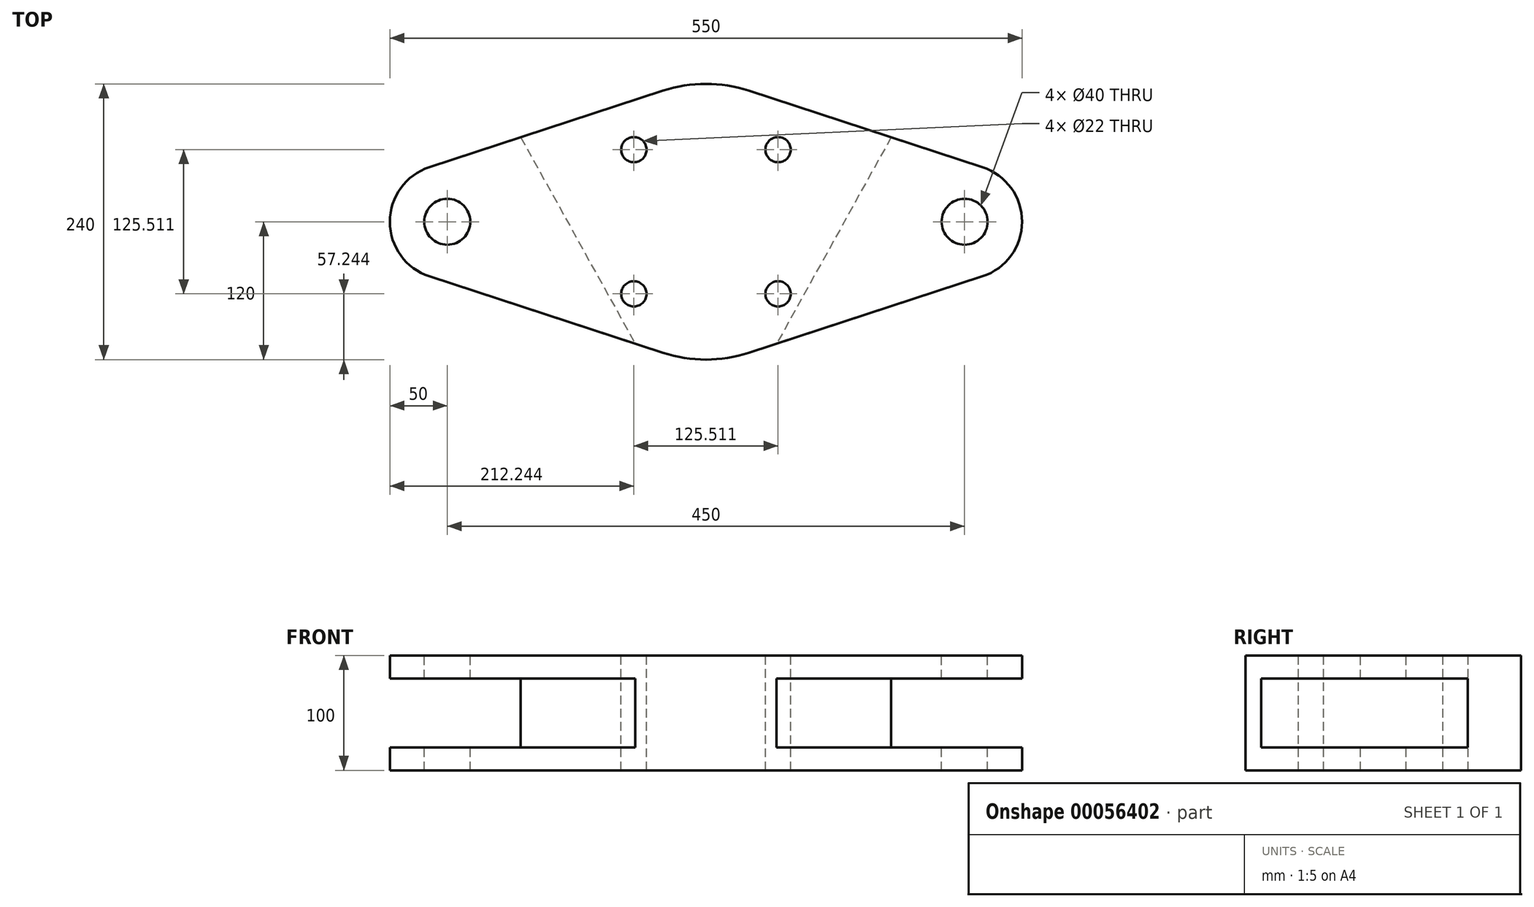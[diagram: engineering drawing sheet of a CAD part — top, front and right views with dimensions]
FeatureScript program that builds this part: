
annotation { "Feature Type Name" : "Feature", "Feature Type Description" : "" }
export const myFeature = defineFeature(function(context is Context, id is Id, definition is map)
    precondition{}
    {
        {
            var Q0;
            Q0=qCreatedBy(makeId("Top.planeOp"),FACE);
            var sketch = newSketch(context, id + "F0", { "sketchPlane" : qUnion([Q0])});
            skArc(sketch, "E0", {"start": v(37.33, 114.04) * mm, "mid": v(0, 120) * mm, "end": v(-37.33, 114.04) * mm});
            skLineSegment(sketch, "E1", {"start": v(0, -118.78) * mm, "end": v(0, 115.8) * mm, "construction": true});
            skArc(sketch, "E2", {"start": v(240.56, -47.52) * mm, "mid": v(275, 0) * mm, "end": v(240.56, 47.52) * mm});
            skLineSegment(sketch, "E3", {"start": v(37.33, 114.04) * mm, "end": v(240.56, 47.52) * mm});
            skLineSegment(sketch, "E4", {"start": v(37.33, -114.04) * mm, "end": v(240.56, -47.52) * mm});
            skLineSegment(sketch, "E5.MirrorCS", {"start": v(-37.33, 114.04) * mm, "end": v(-240.56, 47.52) * mm});
            skArc(sketch, "E6.MirrorCS", {"start": v(-240.56, -47.52) * mm, "mid": v(-275, 0) * mm, "end": v(-240.56, 47.52) * mm});
            skLineSegment(sketch, "E7.MirrorCS", {"start": v(-37.33, -114.04) * mm, "end": v(-240.56, -47.52) * mm});
            skArc(sketch, "E8.trimOffspring", {"start": v(-37.33, -114.04) * mm, "mid": v(0, -120) * mm, "end": v(37.33, -114.04) * mm});
            skLineSegment(sketch, "E9", {"start": v(-225, 0) * mm, "end": v(225, 0) * mm, "construction": true});
            skCircle(sketch, "E10", {"center": v(225, 0) * mm, "radius": 20 * mm});
            skCircle(sketch, "E11", {"center": v(0, 0) * mm, "radius": 88.75 * mm, "construction": true});
            skLineSegment(sketch, "E12", {"start": v(0, 0) * mm, "end": v(79.17, 79.17) * mm, "construction": true});
            skCircle(sketch, "E13", {"center": v(62.76, 62.76) * mm, "radius": 11 * mm});
            skCircle(sketch, "E14.1.0", {"center": v(-62.76, 62.76) * mm, "radius": 11 * mm});
            skCircle(sketch, "E14.2.0", {"center": v(-62.76, -62.76) * mm, "radius": 11 * mm});
            skCircle(sketch, "E14.3.0", {"center": v(62.76, -62.76) * mm, "radius": 11 * mm});
            skPoint(sketch, "E15", {"position": v(61.5, -106.13) * mm});
            skLineSegment(sketch, "E16", {"start": v(61.5, -106.13) * mm, "end": v(170.51, 90.53) * mm, "construction": true});
            skPoint(sketch, "E17.MirrorP", {"position": v(-61.5, -106.13) * mm});
            skLineSegment(sketch, "E18.MirrorCS", {"start": v(-61.5, -106.13) * mm, "end": v(-170.51, 90.53) * mm, "construction": true});
            skCircle(sketch, "E19.MirrorC", {"center": v(-225, 0) * mm, "radius": 20 * mm});
            skSolve(sketch);
        }
        {
            var Q0;
            Q0=makeQuery(id+"F0.imprint","IMPRINT",FACE,{"disambiguationData":[TD([[makeQuery(id+"F0.imprint","IMPRINT",EDGE,{"derivedFrom":sQuery(id+"F0.wireOp",EDGE,"E0")}),1.0]])]});
            extrude(context, id + "F1", {"entities" : qUnion([Q0]), "oppositeDirection" : true, "depth" : 100 * mm});
        }
        {
            var Q0;
            Q0=qCreatedBy(makeId("Right.planeOp"),FACE);
            var Q1;
            Q1=sQuery(id+"F0.wireOp",EDGE,"E16");
            cPlane(context, id + "F2", {"entities" : qUnion([Q0, Q1]), "cplaneType" : CPlaneType.LINE_ANGLE, "offset" : 150 * mm, "angle" : 0 * degree, "width" : 150 * mm, "height" : 150 * mm});
        }
        {
            var Q0;
            Q0=qCreatedBy(makeId("Right.planeOp"),FACE);
            var Q1;
            Q1=sQuery(id+"F0.wireOp",EDGE,"E18.MirrorCS");
            cPlane(context, id + "F3", {"entities" : qUnion([Q0, Q1]), "cplaneType" : CPlaneType.LINE_ANGLE, "offset" : 150 * mm, "angle" : 0 * degree, "width" : 150 * mm, "height" : 150 * mm});
        }
        {
            var Q0;
            Q0=qCreatedBy(makeId("Right.planeOp"),FACE);
            cPlane(context, id + "F4", {"entities" : qUnion([Q0]), "cplaneType" : CPlaneType.OFFSET, "offset" : 275 * mm, "width" : 150 * mm, "height" : 150 * mm});
        }
        {
            var Q0;
            Q0=qCreatedBy(makeId("Right.planeOp"),FACE);
            cPlane(context, id + "F5", {"entities" : qUnion([Q0]), "cplaneType" : CPlaneType.OFFSET, "offset" : 275 * mm, "oppositeDirection" : true, "width" : 150 * mm, "height" : 150 * mm});
        }
        {
            var Q0;
            Q0=qCreatedBy(id+"F4.planeOp",FACE);
            var sketch = newSketch(context, id + "F6", { "sketchPlane" : qUnion([Q0])});
            skLineSegment(sketch, "E20.bottom", {"start": v(120, -80) * mm, "end": v(-120, -80) * mm});
            skLineSegment(sketch, "E20.top", {"start": v(120, -20) * mm, "end": v(-120, -20) * mm});
            skLineSegment(sketch, "E20.left", {"start": v(120, -80) * mm, "end": v(120, -20) * mm});
            skLineSegment(sketch, "E20.right", {"start": v(-120, -80) * mm, "end": v(-120, -20) * mm});
            skSolve(sketch);
        }
        {
            var Q0;
            Q0=makeQuery(id+"F6.imprint","IMPRINT",FACE,{"disambiguationData":[TD([[makeQuery(id+"F6.imprint","IMPRINT",EDGE,{"derivedFrom":sQuery(id+"F6.wireOp",EDGE,"E20.bottom")}),-1.0]])]});
            var Q1;
            Q1=qCreatedBy(id+"F2.planeOp",FACE);
            extrude(context, id + "F7", {"entities" : qUnion([Q0]), "operationType" : NewBodyOperationType.REMOVE, "endBound" : BoundingType.UP_TO_SURFACE, "oppositeDirection" : true, "endBoundEntityFace" : qUnion([Q1]), "depth" : 25 * mm});
        }
        {
            var Q0;
            Q0=qCreatedBy(id+"F5.planeOp",FACE);
            var sketch = newSketch(context, id + "F8", { "sketchPlane" : qUnion([Q0])});
            skLineSegment(sketch, "E21.0.0", {"start": v(-120, -80) * mm, "end": v(120, -80) * mm});
            skLineSegment(sketch, "E21.0.1", {"start": v(120, -80) * mm, "end": v(120, -20) * mm});
            skLineSegment(sketch, "E21.0.2", {"start": v(120, -20) * mm, "end": v(-120, -20) * mm});
            skLineSegment(sketch, "E21.0.3", {"start": v(-120, -20) * mm, "end": v(-120, -80) * mm});
            skSolve(sketch);
        }
        {
            var Q0;
            Q0=makeQuery(id+"F8.imprint","IMPRINT",FACE,{"disambiguationData":[TD([[makeQuery(id+"F8.imprint","IMPRINT",EDGE,{"derivedFrom":sQuery(id+"F8.wireOp",EDGE,"E21.0.0")}),1.0]])]});
            var Q1;
            Q1=qCreatedBy(id+"F3.planeOp",FACE);
            extrude(context, id + "F9", {"entities" : qUnion([Q0]), "operationType" : NewBodyOperationType.REMOVE, "endBound" : BoundingType.UP_TO_SURFACE, "endBoundEntityFace" : qUnion([Q1]), "depth" : 75.99 * mm});
        }
    });
